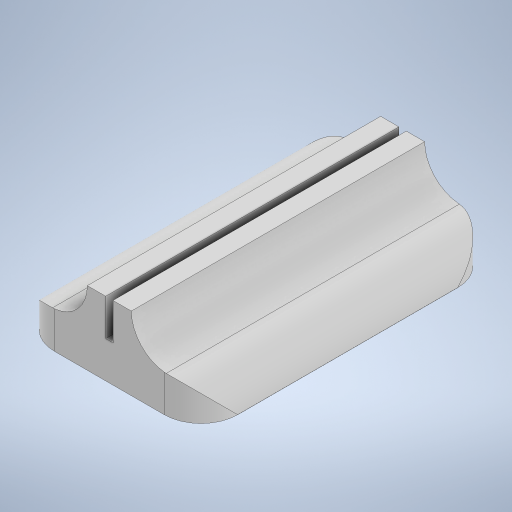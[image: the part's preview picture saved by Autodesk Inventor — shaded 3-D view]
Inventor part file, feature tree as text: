
AUTODESK INVENTOR PART (.ipt)
format: ipt  version: 2024.2 (Build 282272000, 272)  size: 272,896 bytes
history: native  units: mm
features: extrude x2, fillet x2, sketch x2
ambient origin geometry x8: Origin, YZ Plane, XZ Plane, XY Plane, X Axis, Y Axis, Z Axis, Center Point
bodies: Solid1 (feature_tree)
feature tree (6):
  extrude  "Extrusion1"  Depth=80.0mm
  extrude  "Extrusion2"  Depth=10.0mm
  fillet  "Fillet1"  Radius=5.0mm
  fillet  "Fillet2"  Radius=2.0mm
  sketch  "Sketch1"  dims[d0=50.0mm d1=80.0mm]
  sketch  "Sketch2"  dims[d2=10.0mm d3=0.0mm d7=5.0mm d8=5.0mm d9=2.0mm d10=19.0mm d11=10.0mm d12=0.0mm d13=10.0mm d14=10.0mm]
